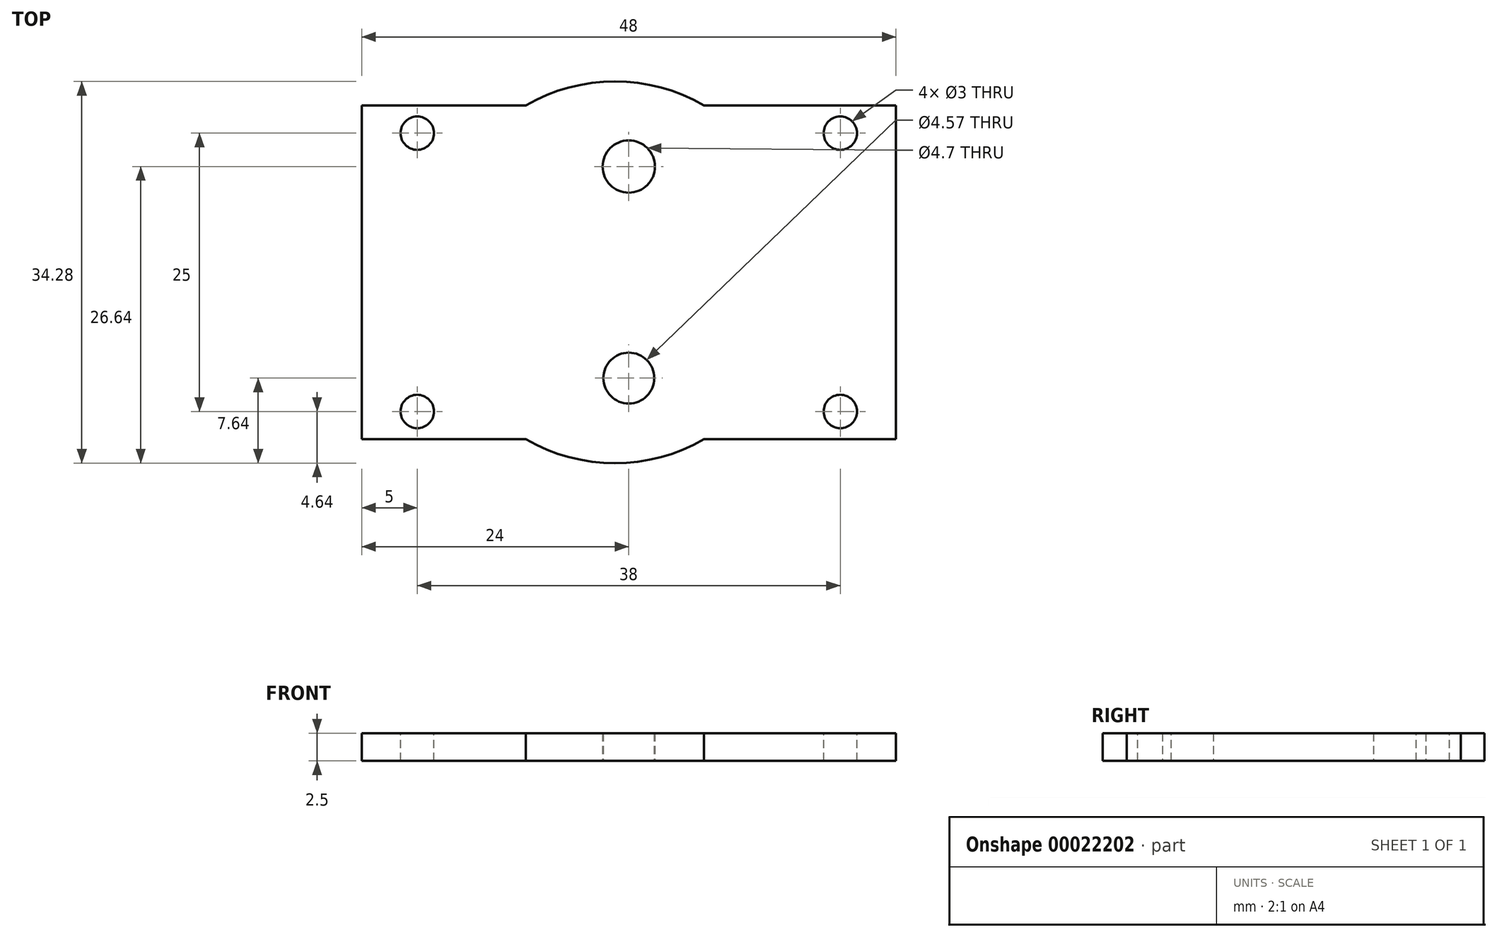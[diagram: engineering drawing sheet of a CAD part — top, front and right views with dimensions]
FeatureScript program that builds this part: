
annotation { "Feature Type Name" : "Feature", "Feature Type Description" : "" }
export const myFeature = defineFeature(function(context is Context, id is Id, definition is map)
    precondition{}
    {
        {
            var Q0;
            Q0=qCreatedBy(makeId("Top.planeOp"),FACE);
            var sketch = newSketch(context, id + "F0", { "sketchPlane" : qUnion([Q0])});
            skPoint(sketch, "E0.rect.middle", {"position": v(0, 0) * mm});
            skCircle(sketch, "E1", {"center": v(0, 0) * mm, "radius": 9.5 * mm, "construction": true});
            skCircle(sketch, "E2", {"center": v(0, 0) * mm, "radius": 14 * mm, "construction": true});
            skCircle(sketch, "E3", {"center": v(0, 9.5) * mm, "radius": 2.35 * mm});
            skCircle(sketch, "E4", {"center": v(0, -9.5) * mm, "radius": 2.28 * mm});
            skSolve(sketch);
        }
        {
            var Q0;
            Q0=qCreatedBy(makeId("Top.planeOp"),FACE);
            var sketch = newSketch(context, id + "F1", { "sketchPlane" : qUnion([Q0])});
            skLineSegment(sketch, "E5.rect.bottom", {"start": v(24, -15) * mm, "end": v(6.76, -15) * mm});
            skLineSegment(sketch, "E5.rect.top", {"start": v(24, 15) * mm, "end": v(6.76, 15) * mm});
            skLineSegment(sketch, "E5.rect.left", {"start": v(24, -15) * mm, "end": v(24, 15) * mm});
            skLineSegment(sketch, "E5.rect.right", {"start": v(-24, -15) * mm, "end": v(-24, 15) * mm});
            skPoint(sketch, "E5.rect.middle", {"position": v(0, 0) * mm});
            skArc(sketch, "E6", {"start": v(6.76, 15) * mm, "mid": v(-1.24, 17.14) * mm, "end": v(-9.25, 15) * mm});
            skArc(sketch, "E7.MirrorCS", {"start": v(6.76, -15) * mm, "mid": v(-1.24, -17.14) * mm, "end": v(-9.25, -15) * mm});
            skLineSegment(sketch, "E8.trimOffspring", {"start": v(-9.25, 15) * mm, "end": v(-24, 15) * mm});
            skLineSegment(sketch, "E9.trimOffspring", {"start": v(-9.25, -15) * mm, "end": v(-24, -15) * mm});
            skSolve(sketch);
        }
        {
            var Q0;
            Q0 = qSketchRegion(id + "F1", true);
            extrude(context, id + "F2", {"entities" : qUnion([Q0]), "depth" : 2.5 * mm});
        }
        {
            var Q0;
            Q0 = qSketchRegion(id + "F0", true);
            extrude(context, id + "F3", {"entities" : qUnion([Q0]), "operationType" : NewBodyOperationType.REMOVE, "endBound" : BoundingType.UP_TO_NEXT, "depth" : 25 * mm});
        }
        {
            var Q0;
            Q0=makeQuery(id+"F2.opExtrude","CAP_FACE",FACE,{"disambiguationData":[OSD([sQuery(id+"F1.wireOp",EDGE,"E5.rect.bottom"),sQuery(id+"F1.wireOp",EDGE,"E5.rect.top"),sQuery(id+"F1.wireOp",EDGE,"E5.rect.left"),sQuery(id+"F1.wireOp",EDGE,"E5.rect.right"),sQuery(id+"F1.wireOp",EDGE,"E6"),sQuery(id+"F1.wireOp",EDGE,"E7.MirrorCS"),sQuery(id+"F1.wireOp",EDGE,"E8.trimOffspring"),sQuery(id+"F1.wireOp",EDGE,"E9.trimOffspring")])],"isStart":false});
            var sketch = newSketch(context, id + "F4", { "sketchPlane" : qUnion([Q0])});
            skCircle(sketch, "E10", {"center": v(-19, 12.5) * mm, "radius": 1.5 * mm});
            skCircle(sketch, "E11.MirrorC", {"center": v(-19, -12.5) * mm, "radius": 1.5 * mm});
            skCircle(sketch, "E12.MirrorC", {"center": v(19, 12.5) * mm, "radius": 1.5 * mm});
            skCircle(sketch, "E13.MirrorC", {"center": v(19, -12.5) * mm, "radius": 1.5 * mm});
            skSolve(sketch);
        }
        {
            var Q0;
            Q0 = qSketchRegion(id + "F4", true);
            extrude(context, id + "F5", {"entities" : qUnion([Q0]), "operationType" : NewBodyOperationType.REMOVE, "endBound" : BoundingType.UP_TO_NEXT, "oppositeDirection" : true, "depth" : 25 * mm});
        }
    });
